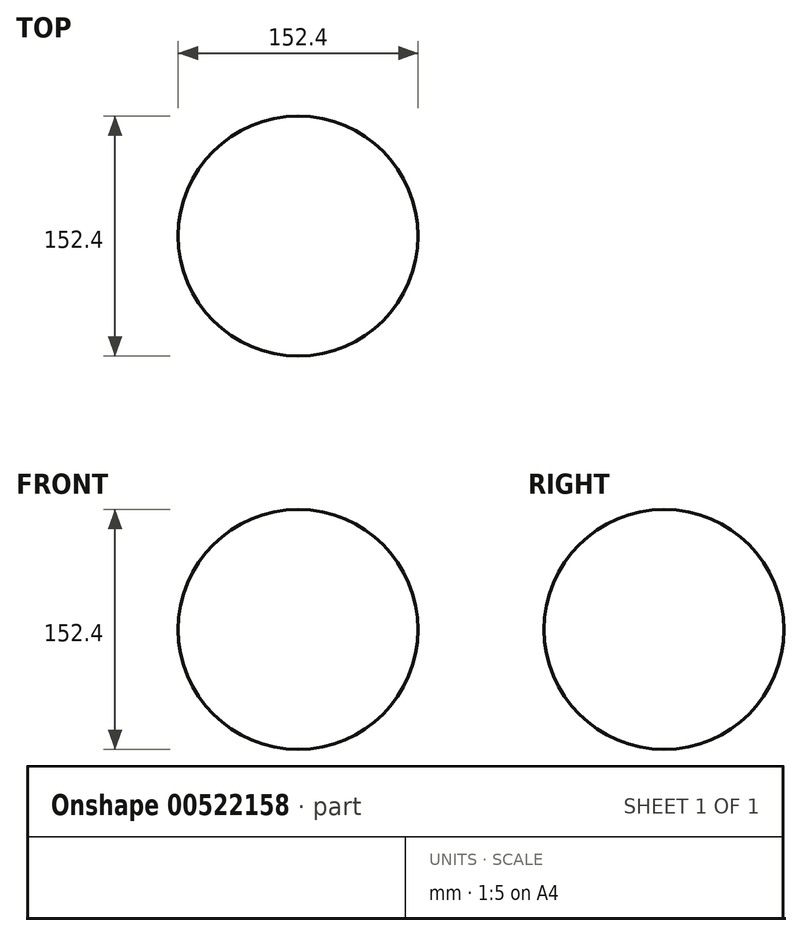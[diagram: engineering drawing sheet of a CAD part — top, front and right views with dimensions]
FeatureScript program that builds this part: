
annotation { "Feature Type Name" : "Feature", "Feature Type Description" : "" }
export const myFeature = defineFeature(function(context is Context, id is Id, definition is map)
    precondition{}
    {
        {
            var Q0;
            Q0=qCreatedBy(makeId("Top.planeOp"),FACE);
            var sketch = newSketch(context, id + "F0", { "sketchPlane" : qUnion([Q0])});
            skLineSegment(sketch, "E0", {"start": v(0, 0) * mm, "end": v(76.2, 0) * mm});
            skLineSegment(sketch, "E1", {"start": v(0, 0) * mm, "end": v(0, 76.2) * mm});
            skArc(sketch, "E2", {"start": v(76.2, 0) * mm, "mid": v(53.88, 53.88) * mm, "end": v(0, 76.2) * mm});
            skLineSegment(sketch, "E3", {"start": v(0, 0) * mm, "end": v(-76.2, 0) * mm});
            skArc(sketch, "E4", {"start": v(0, 76.2) * mm, "mid": v(-53.88, 53.88) * mm, "end": v(-76.2, 0) * mm});
            skSolve(sketch);
        }
        {
            var Q0;
            Q0=makeQuery(id+"F0.imprint","IMPRINT",FACE,{"disambiguationData":[TD([[makeQuery(id+"F0.imprint","IMPRINT",EDGE,{"derivedFrom":sQuery(id+"F0.wireOp",EDGE,"E0")}),1.0]])]});
            var Q1;
            Q1=sQuery(id+"F0.wireOp",EDGE,"E0");
            revolve(context, id + "F1", {"entities" : qUnion([Q0]), "axis" : qUnion([Q1]), "revolveType" : RevolveType.FULL});
        }
        {
            var Q0;
            Q0=makeQuery(id+"F0.imprint","IMPRINT",FACE,{"disambiguationData":[TD([[makeQuery(id+"F0.imprint","IMPRINT",EDGE,{"derivedFrom":sQuery(id+"F0.wireOp",EDGE,"E0")}),1.0]])]});
            var Q1;
            Q1=sQuery(id+"F0.wireOp",EDGE,"E0");
            revolve(context, id + "F2", {"entities" : qUnion([Q0]), "axis" : qUnion([Q1]), "revolveType" : RevolveType.FULL});
        }
        {
            var Q0;
            Q0=makeQuery(id+"F0.imprint","IMPRINT",FACE,{"disambiguationData":[TD([[makeQuery(id+"F0.imprint","IMPRINT",EDGE,{"derivedFrom":sQuery(id+"F0.wireOp",EDGE,"E1")}),1.0]])]});
            var Q1;
            Q1=sQuery(id+"F0.wireOp",EDGE,"E3");
            revolve(context, id + "F3", {"operationType" : NewBodyOperationType.ADD, "entities" : qUnion([Q0]), "axis" : qUnion([Q1]), "revolveType" : RevolveType.FULL});
        }
    });
